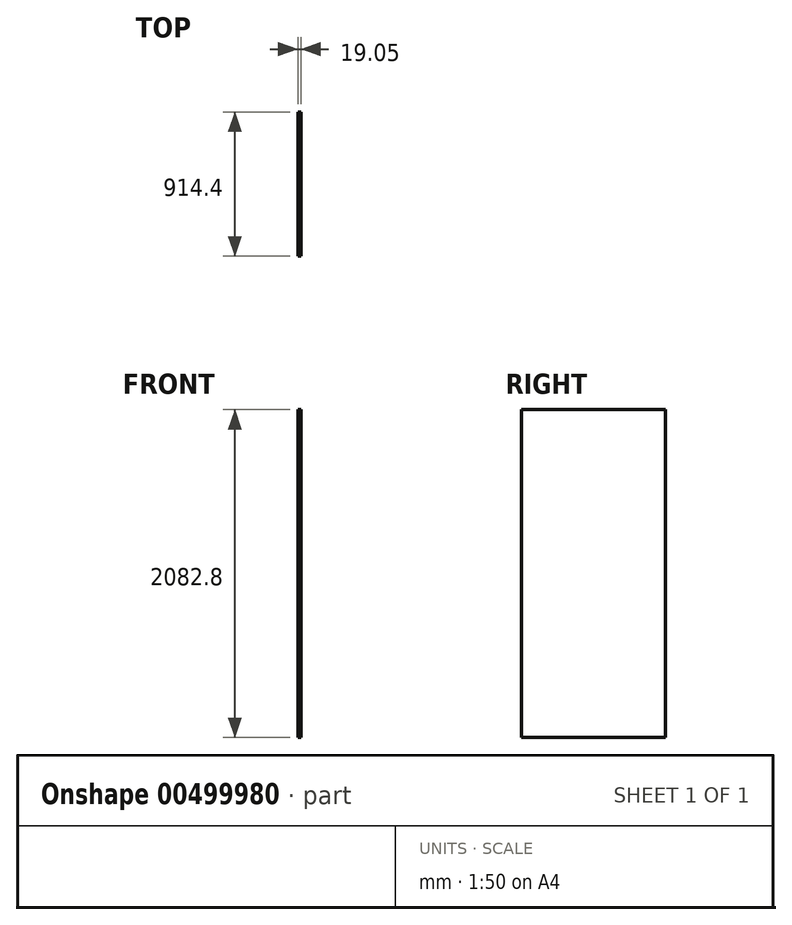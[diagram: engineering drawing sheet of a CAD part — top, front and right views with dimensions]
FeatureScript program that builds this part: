
annotation { "Feature Type Name" : "Feature", "Feature Type Description" : "" }
export const myFeature = defineFeature(function(context is Context, id is Id, definition is map)
    precondition{}
    {
        {
            var Q0;
            Q0=qCreatedBy(makeId("Right.planeOp"),FACE);
            var sketch = newSketch(context, id + "F0", { "sketchPlane" : qUnion([Q0])});
            skLineSegment(sketch, "E0.bottom", {"start": v(-457.2, 1041.4) * mm, "end": v(457.2, 1041.4) * mm});
            skLineSegment(sketch, "E0.top", {"start": v(-457.2, -1041.4) * mm, "end": v(457.2, -1041.4) * mm});
            skLineSegment(sketch, "E0.left", {"start": v(-457.2, 1041.4) * mm, "end": v(-457.2, -1041.4) * mm});
            skLineSegment(sketch, "E0.right", {"start": v(457.2, 1041.4) * mm, "end": v(457.2, -1041.4) * mm});
            skPoint(sketch, "E0.middle", {"position": v(0, 0) * mm});
            skLineSegment(sketch, "E1.bottom", {"start": v(-457.2, -1041.4) * mm, "end": v(762, -1041.4) * mm});
            skSolve(sketch);
        }
        {
            var Q0;
            Q0=qSketchRegion(id+"F0",true);
            extrude(context, id + "F1", {"entities" : qUnion([Q0]), "depth" : 19.05 * mm, "offsetDistance" : 25.4 * mm});
        }
    });
